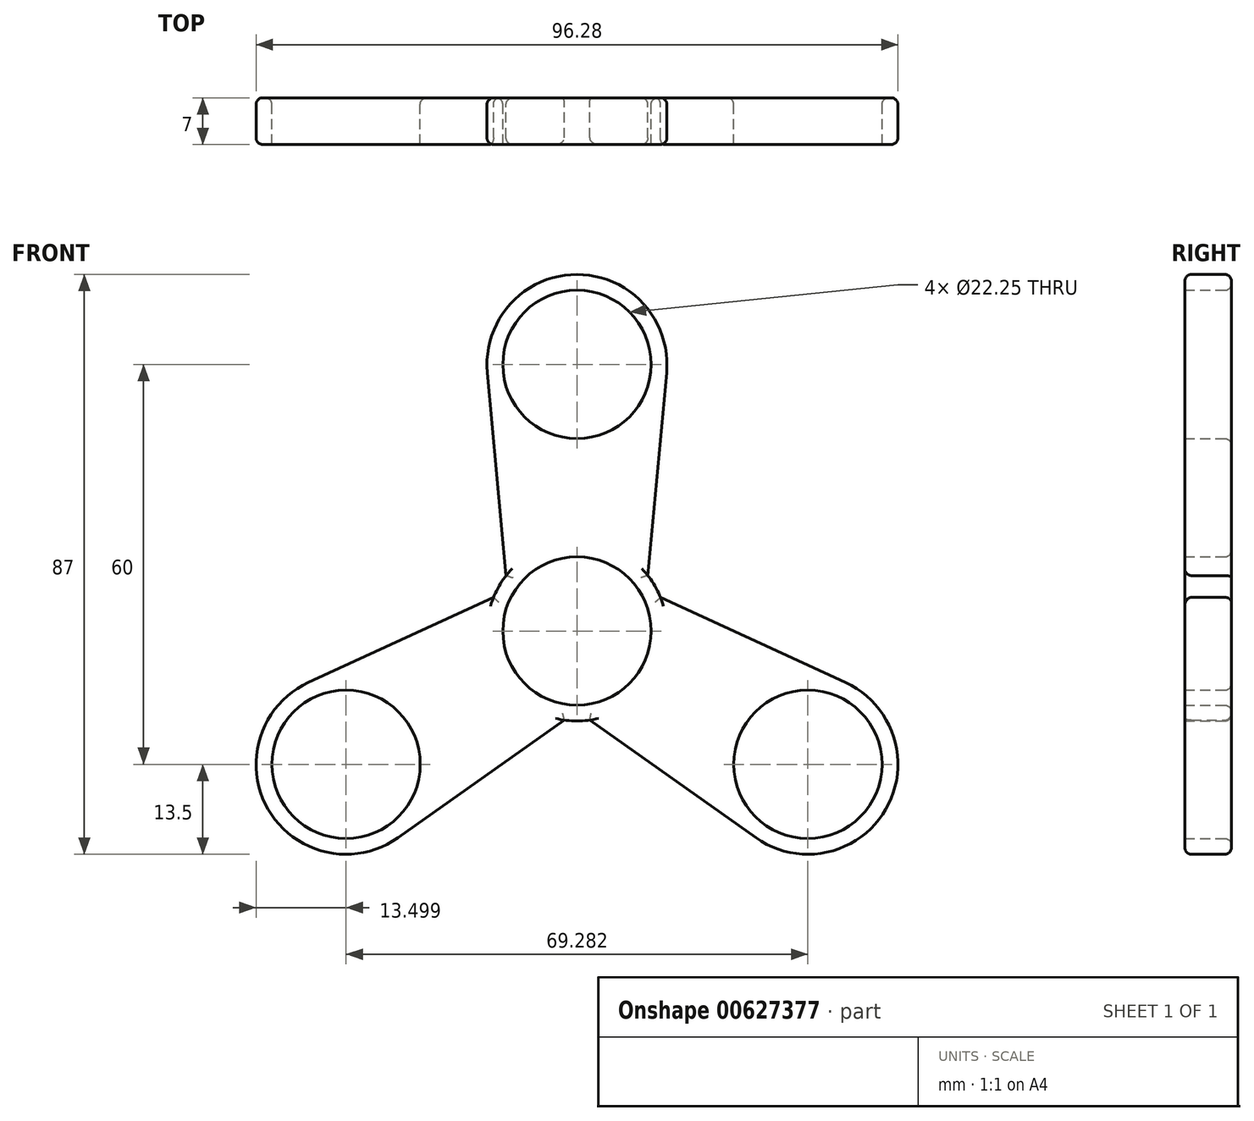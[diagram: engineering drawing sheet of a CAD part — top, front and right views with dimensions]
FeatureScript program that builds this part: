
annotation { "Feature Type Name" : "Feature", "Feature Type Description" : "" }
export const myFeature = defineFeature(function(context is Context, id is Id, definition is map)
    precondition{}
    {
        {
            var Q0;
            Q0=qCreatedBy(makeId("Front.planeOp"),FACE);
            var sketch = newSketch(context, id + "F0", { "sketchPlane" : qUnion([Q0])});
            skCircle(sketch, "E0", {"center": v(0, 0) * mm, "radius": 11.12 * mm});
            skCircle(sketch, "E1", {"center": v(0, 0) * mm, "radius": 13.5 * mm});
            skCircle(sketch, "E2", {"center": v(-34.64, -20) * mm, "radius": 11.12 * mm});
            skCircle(sketch, "E3", {"center": v(34.64, -20) * mm, "radius": 11.12 * mm});
            skCircle(sketch, "E4", {"center": v(0, 40) * mm, "radius": 11.12 * mm});
            skCircle(sketch, "E5", {"center": v(0, 40) * mm, "radius": 13.5 * mm});
            skCircle(sketch, "E6", {"center": v(-34.64, -20) * mm, "radius": 13.5 * mm});
            skCircle(sketch, "E7", {"center": v(34.64, -20) * mm, "radius": 13.5 * mm});
            skArc(sketch, "E8", {"start": v(10.63, 8.32) * mm, "mid": v(0, 16.5) * mm, "end": v(-10.63, 8.32) * mm});
            skLineSegment(sketch, "E9", {"start": v(0, 0) * mm, "end": v(0, 21.17) * mm});
            skArc(sketch, "E10", {"start": v(-12.52, 5.05) * mm, "mid": v(-14.29, -8.25) * mm, "end": v(-1.89, -13.37) * mm});
            skArc(sketch, "E11", {"start": v(1.89, -13.37) * mm, "mid": v(14.29, -8.25) * mm, "end": v(12.52, 5.05) * mm});
            skLineSegment(sketch, "E12", {"start": v(10.63, 8.32) * mm, "end": v(13.44, 38.76) * mm});
            skLineSegment(sketch, "E13", {"start": v(-10.63, 8.32) * mm, "end": v(-13.44, 38.76) * mm});
            skLineSegment(sketch, "E14", {"start": v(-12.52, 5.05) * mm, "end": v(-40.29, -7.74) * mm});
            skLineSegment(sketch, "E15", {"start": v(-1.89, -13.37) * mm, "end": v(-26.84, -31.02) * mm});
            skLineSegment(sketch, "E16", {"start": v(1.89, -13.37) * mm, "end": v(26.84, -31.02) * mm});
            skLineSegment(sketch, "E17", {"start": v(12.52, 5.05) * mm, "end": v(40.29, -7.74) * mm});
            skLineSegment(sketch, "E18", {"start": v(10.63, 8.32) * mm, "end": v(11.55, 18.28) * mm});
            skLineSegment(sketch, "E19", {"start": v(12.52, 5.05) * mm, "end": v(21.6, 0.87) * mm});
            skLineSegment(sketch, "E20", {"start": v(-10.63, 8.32) * mm, "end": v(-11.55, 18.28) * mm});
            skLineSegment(sketch, "E21", {"start": v(-12.52, 5.05) * mm, "end": v(-21.6, 0.87) * mm});
            skLineSegment(sketch, "E22", {"start": v(-1.89, -13.37) * mm, "end": v(-10.05, -19.14) * mm});
            skLineSegment(sketch, "E23", {"start": v(1.89, -13.37) * mm, "end": v(10.05, -19.14) * mm});
            skArc(sketch, "E24", {"start": v(-10.05, -19.14) * mm, "mid": v(0, -21.62) * mm, "end": v(10.05, -19.14) * mm});
            skArc(sketch, "E25.trimOffspring", {"start": v(21.6, 0.87) * mm, "mid": v(18.72, 10.81) * mm, "end": v(11.55, 18.28) * mm});
            skArc(sketch, "E26.trimOffspring", {"start": v(-11.55, 18.28) * mm, "mid": v(-18.72, 10.81) * mm, "end": v(-21.6, 0.87) * mm});
            skSolve(sketch);
        }
        {
            var Q0;
            {var subQ4=sQuery(id+"F0.wireOp",EDGE,"E12");Q0=makeQuery(id+"F0.imprint","IMPRINT",FACE,{"disambiguationData":[TD([[makeQuery(id+"F0.imprint","IMPRINT",EDGE,{"derivedFrom":subQ4}),1.0]])]});}
            var Q1;
            Q1=makeQuery(id+"F0.imprint","IMPRINT",FACE,{"disambiguationData":[TD([[makeQuery(id+"F0.imprint","IMPRINT",EDGE,{"derivedFrom":sQuery(id+"F0.wireOp",EDGE,"E10")}),-1.0]])]});
            var Q2;
            {var subQ0=sQuery(id+"F0.wireOp",EDGE,"E11");Q2=makeQuery(id+"F0.imprint","IMPRINT",FACE,{"disambiguationData":[TD([[makeQuery(id+"F0.imprint","IMPRINT",EDGE,{"derivedFrom":subQ0}),1.0]])]});}
            var Q3;
            {var subQ0=sQuery(id+"F0.wireOp",EDGE,"E10");Q3=makeQuery(id+"F0.imprint","IMPRINT",FACE,{"disambiguationData":[TD([[makeQuery(id+"F0.imprint","IMPRINT",EDGE,{"derivedFrom":subQ0}),1.0]])]});}
            var Q4;
            {var subQ1=sQuery(id+"F0.wireOp",EDGE,"E1");var subQ3=sQuery(id+"F0.wireOp",EDGE,"E9");var subQ4=makeQuery(id+"F0.imprint","INTERSECT",VERTEX,{"derivedFrom":[subQ1,subQ3]});Q4=makeQuery(id+"F0.imprint","IMPRINT",FACE,{"disambiguationData":[TD([[makeQuery(id+"F0.imprint","IMPRINT",EDGE,{"disambiguationData":[TD([[subQ4,-1.0]])],"derivedFrom":subQ3}),-1.0]])]});}
            var Q5;
            Q5=makeQuery(id+"F0.imprint","IMPRINT",FACE,{"disambiguationData":[TD([[makeQuery(id+"F0.imprint","IMPRINT",EDGE,{"derivedFrom":sQuery(id+"F0.wireOp",EDGE,"E11")}),-1.0]])]});
            var Q6;
            {var subQ1=sQuery(id+"F0.wireOp",EDGE,"E1");var subQ3=sQuery(id+"F0.wireOp",EDGE,"E9");var subQ4=makeQuery(id+"F0.imprint","INTERSECT",VERTEX,{"derivedFrom":[subQ1,subQ3]});Q6=makeQuery(id+"F0.imprint","IMPRINT",FACE,{"disambiguationData":[TD([[makeQuery(id+"F0.imprint","IMPRINT",EDGE,{"disambiguationData":[TD([[subQ4,-1.0]])],"derivedFrom":subQ3}),1.0]])]});}
            var Q7;
            Q7=makeQuery(id+"F0.imprint","IMPRINT",FACE,{"disambiguationData":[TD([[makeQuery(id+"F0.imprint","IMPRINT",EDGE,{"derivedFrom":sQuery(id+"F0.wireOp",EDGE,"E4")}),-1.0]])]});
            var Q8;
            Q8=makeQuery(id+"F0.imprint","IMPRINT",FACE,{"disambiguationData":[TD([[makeQuery(id+"F0.imprint","IMPRINT",EDGE,{"derivedFrom":sQuery(id+"F0.wireOp",EDGE,"E0")}),-1.0]])]});
            var Q9;
            Q9=makeQuery(id+"F0.imprint","IMPRINT",FACE,{"disambiguationData":[TD([[makeQuery(id+"F0.imprint","IMPRINT",EDGE,{"derivedFrom":sQuery(id+"F0.wireOp",EDGE,"E2")}),-1.0]])]});
            var Q10;
            Q10=makeQuery(id+"F0.imprint","IMPRINT",FACE,{"disambiguationData":[TD([[makeQuery(id+"F0.imprint","IMPRINT",EDGE,{"derivedFrom":sQuery(id+"F0.wireOp",EDGE,"E3")}),-1.0]])]});
            var Q11;
            {var subQ0=sQuery(id+"F0.wireOp",EDGE,"E20");Q11=makeQuery(id+"F0.imprint","IMPRINT",FACE,{"disambiguationData":[TD([[makeQuery(id+"F0.imprint","IMPRINT",EDGE,{"derivedFrom":subQ0}),1.0]])]});}
            var Q12;
            {var subQ0=sQuery(id+"F0.wireOp",EDGE,"E18");Q12=makeQuery(id+"F0.imprint","IMPRINT",FACE,{"disambiguationData":[TD([[makeQuery(id+"F0.imprint","IMPRINT",EDGE,{"derivedFrom":subQ0}),-1.0]])]});}
            var Q13;
            {var subQ0=sQuery(id+"F0.wireOp",EDGE,"E22");Q13=makeQuery(id+"F0.imprint","IMPRINT",FACE,{"disambiguationData":[TD([[makeQuery(id+"F0.imprint","IMPRINT",EDGE,{"derivedFrom":subQ0}),1.0]])]});}
            extrude(context, id + "F1", {"entities" : qUnion([Q0, Q1, Q2, Q3, Q4, Q5, Q6, Q7, Q8, Q9, Q10, Q11, Q12, Q13]), "depth" : 7 * mm, "offsetDistance" : 25 * mm});
        }
        {
            var Q0;
            Q0=makeQuery(id+"F1.opExtrude","CAP_EDGE",EDGE,{"disambiguationData":[OSD([sQuery(id+"F0.wireOp",EDGE,"E12")])],"isStart":false});
            var Q1;
            Q1=makeQuery(id+"F1.opExtrude","CAP_EDGE",EDGE,{"disambiguationData":[OSD([sQuery(id+"F0.wireOp",EDGE,"E14")])],"isStart":false});
            var Q2;
            Q2=makeQuery(id+"F1.opExtrude","CAP_EDGE",EDGE,{"disambiguationData":[OSD([sQuery(id+"F0.wireOp",EDGE,"E16")])],"isStart":false});
            var Q3;
            Q3=makeQuery(id+"F1.opExtrude","CAP_EDGE",EDGE,{"disambiguationData":[OSD([sQuery(id+"F0.wireOp",EDGE,"85552c91-ca7e-47ec-b4b7-672efefcc70b.trimOffspring")])],"isStart":false});
            var Q4;
            Q4=makeQuery(id+"F1.opExtrude","CAP_EDGE",EDGE,{"disambiguationData":[OSD([sQuery(id+"F0.wireOp",EDGE,"552f1abf-b9a5-49fc-ac39-f913d654a642.trimOffspring")])],"isStart":false});
            var Q5;
            Q5=makeQuery(id+"F1.opExtrude","CAP_EDGE",EDGE,{"disambiguationData":[OSD([sQuery(id+"F0.wireOp",EDGE,"DNbiW4gv-E8eL-lTfj-EAYC-LwjJ7cAAOpNq")])],"isStart":false});
            var Q6;
            Q6=makeQuery(id+"F1.opExtrude","CAP_EDGE",EDGE,{"disambiguationData":[OSD([sQuery(id+"F0.wireOp",EDGE,"E15")])],"isStart":true});
            var Q7;
            Q7=makeQuery(id+"F1.opExtrude","CAP_FACE",FACE,{"disambiguationData":[OSD([sQuery(id+"F0.wireOp",EDGE,"E0"),sQuery(id+"F0.wireOp",EDGE,"E2"),sQuery(id+"F0.wireOp",EDGE,"E3"),sQuery(id+"F0.wireOp",EDGE,"E4"),sQuery(id+"F0.wireOp",EDGE,"E5"),sQuery(id+"F0.wireOp",EDGE,"E6"),sQuery(id+"F0.wireOp",EDGE,"E7"),sQuery(id+"F0.wireOp",EDGE,"E12"),sQuery(id+"F0.wireOp",EDGE,"E13"),sQuery(id+"F0.wireOp",EDGE,"E14"),sQuery(id+"F0.wireOp",EDGE,"E15"),sQuery(id+"F0.wireOp",EDGE,"E16"),sQuery(id+"F0.wireOp",EDGE,"E17"),sQuery(id+"F0.wireOp",EDGE,"DNbiW4gv-E8eL-lTfj-EAYC-LwjJ7cAAOpNq"),sQuery(id+"F0.wireOp",EDGE,"85552c91-ca7e-47ec-b4b7-672efefcc70b.trimOffspring"),sQuery(id+"F0.wireOp",EDGE,"552f1abf-b9a5-49fc-ac39-f913d654a642.trimOffspring")])],"isStart":true});
            var Q8;
            Q8=makeQuery(id+"F1.opExtrude","CAP_EDGE",EDGE,{"disambiguationData":[OSD([sQuery(id+"F0.wireOp",EDGE,"E12")])],"isStart":true});
            var Q9;
            Q9=makeQuery(id+"F1.opExtrude","CAP_EDGE",EDGE,{"disambiguationData":[OSD([sQuery(id+"F0.wireOp",EDGE,"E16")])],"isStart":true});
            var Q10;
            Q10=makeQuery(id+"F1.opExtrude","CAP_EDGE",EDGE,{"disambiguationData":[OSD([sQuery(id+"F0.wireOp",EDGE,"E13")])],"isStart":true});
            var Q11;
            Q11=makeQuery(id+"F1.opExtrude","CAP_EDGE",EDGE,{"disambiguationData":[OSD([sQuery(id+"F0.wireOp",EDGE,"DNbiW4gv-E8eL-lTfj-EAYC-LwjJ7cAAOpNq")])],"isStart":true});
            var Q12;
            Q12=makeQuery(id+"F1.opExtrude","CAP_EDGE",EDGE,{"disambiguationData":[OSD([sQuery(id+"F0.wireOp",EDGE,"E25.trimOffspring")])],"isStart":false});
            var Q13;
            Q13=makeQuery(id+"F1.opExtrude","CAP_EDGE",EDGE,{"disambiguationData":[OSD([sQuery(id+"F0.wireOp",EDGE,"E24")])],"isStart":false});
            var Q14;
            Q14=makeQuery(id+"F1.opExtrude","CAP_EDGE",EDGE,{"disambiguationData":[OSD([sQuery(id+"F0.wireOp",EDGE,"E26.trimOffspring")])],"isStart":false});
            fillet(context, id + "F2", {"entities" : qUnion([Q0, Q1, Q2, Q3, Q4, Q5, Q6, Q7, Q8, Q9, Q10, Q11, Q12, Q13, Q14]), "radius" : 1 * mm, "tangentPropagation" : true, "allowEdgeOverflow" : false});
        }
    });
